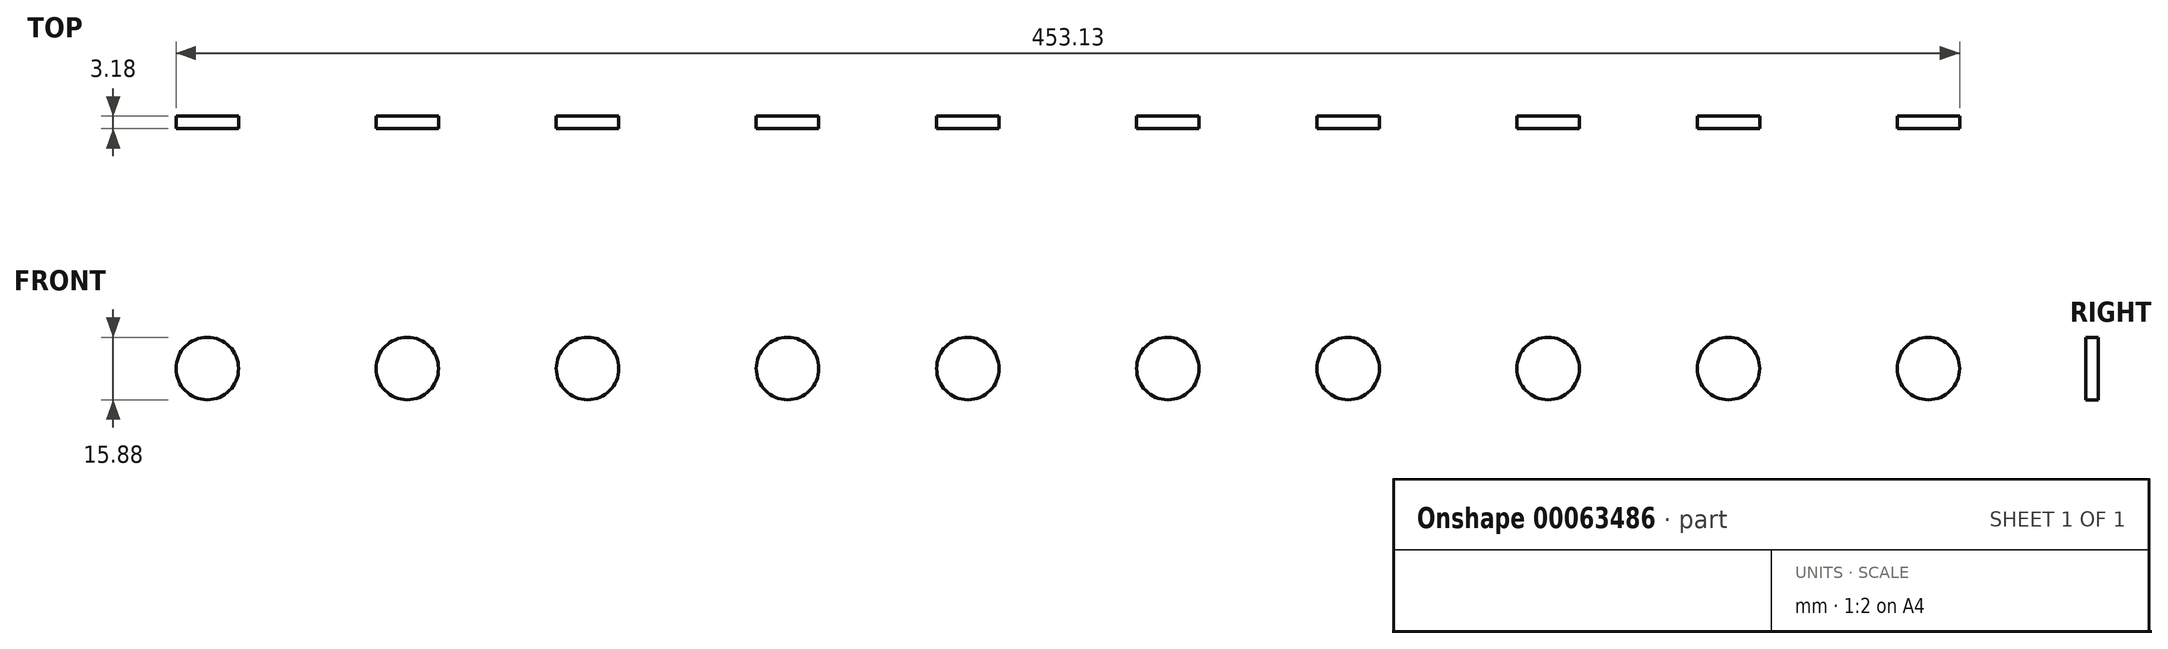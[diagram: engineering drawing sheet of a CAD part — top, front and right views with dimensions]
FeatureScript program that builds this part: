
annotation { "Feature Type Name" : "Feature", "Feature Type Description" : "" }
export const myFeature = defineFeature(function(context is Context, id is Id, definition is map)
    precondition{}
    {
        {
            var Q0;
            Q0=qCreatedBy(makeId("Front.planeOp"),FACE);
            var sketch = newSketch(context, id + "F0", { "sketchPlane" : qUnion([Q0])});
            skLineSegment(sketch, "E0.bottom", {"start": v(-400.95, 39.66) * mm, "end": v(684.9, 39.66) * mm});
            skLineSegment(sketch, "E0.top", {"start": v(-400.95, 14.26) * mm, "end": v(684.9, 14.26) * mm});
            skLineSegment(sketch, "E0.left", {"start": v(-400.95, 39.66) * mm, "end": v(-400.95, 14.26) * mm});
            skLineSegment(sketch, "E0.right", {"start": v(684.9, 39.66) * mm, "end": v(684.9, 14.26) * mm});
            skSolve(sketch);
        }
        {
            var Q0;
            Q0=makeQuery(id+"F0.imprint","IMPRINT",FACE,{"disambiguationData":[TD([[makeQuery(id+"F0.imprint","IMPRINT",EDGE,{"derivedFrom":sQuery(id+"F0.wireOp",EDGE,"E0.bottom")}),-1.0]])]});
            extrude(context, id + "F1", {"entities" : qUnion([Q0]), "depth" : 12.7 * mm});
        }
        {
            var Q0;
            Q0=makeQuery(id+"F1.opExtrude","SWEPT_FACE",FACE,{"disambiguationData":[OSD([sQuery(id+"F0.wireOp",EDGE,"E0.left")])]});
            var sketch = newSketch(context, id + "F2", { "sketchPlane" : qUnion([Q0])});
            skLineSegment(sketch, "E1.0", {"start": v(12.7, 39.66) * mm, "end": v(0, 39.66) * mm});
            skLineSegment(sketch, "E1.1", {"start": v(12.7, 39.66) * mm, "end": v(12.7, 14.26) * mm});
            skLineSegment(sketch, "E1.2", {"start": v(12.7, 14.26) * mm, "end": v(0, 14.26) * mm});
            skLineSegment(sketch, "E2.0", {"start": v(9.53, 36.48) * mm, "end": v(0, 36.48) * mm});
            skLineSegment(sketch, "E2.1", {"start": v(9.53, 36.48) * mm, "end": v(9.53, 17.43) * mm});
            skLineSegment(sketch, "E2.2", {"start": v(9.53, 17.43) * mm, "end": v(0, 17.43) * mm});
            skLineSegment(sketch, "E3.0", {"start": v(0, 39.66) * mm, "end": v(0, 14.26) * mm});
            skSolve(sketch);
        }
        {
            var Q0;
            {var subQ0=sQuery(id+"F2.wireOp",EDGE,"E2.0");Q0=makeQuery(id+"F2.imprint","IMPRINT",FACE,{"disambiguationData":[TD([[makeQuery(id+"F2.imprint","IMPRINT",EDGE,{"derivedFrom":subQ0}),1.0]])]});}
            extrude(context, id + "F3", {"entities" : qUnion([Q0]), "operationType" : NewBodyOperationType.REMOVE, "endBound" : BoundingType.THROUGH_ALL, "oppositeDirection" : true, "depth" : 25.4 * mm});
        }
        {
            var Q0;
            Q0=makeQuery(id+"F1.opExtrude","CAP_FACE",FACE,{"disambiguationData":[OSD([sQuery(id+"F0.wireOp",EDGE,"E0.bottom"),sQuery(id+"F0.wireOp",EDGE,"E0.top"),sQuery(id+"F0.wireOp",EDGE,"E0.left"),sQuery(id+"F0.wireOp",EDGE,"E0.right")])],"isStart":false});
            var sketch = newSketch(context, id + "F4", { "sketchPlane" : qUnion([Q0])});
            skLineSegment(sketch, "E4.0", {"start": v(-400.95, 39.66) * mm, "end": v(-400.95, 14.26) * mm});
            skLineSegment(sketch, "E4.1", {"start": v(-400.95, 39.66) * mm, "end": v(684.9, 39.66) * mm});
            skLineSegment(sketch, "E4.2", {"start": v(-400.95, 14.26) * mm, "end": v(684.9, 14.26) * mm});
            skLineSegment(sketch, "E4.3", {"start": v(684.9, 39.66) * mm, "end": v(684.9, 14.26) * mm});
            skLineSegment(sketch, "E5", {"start": v(-400.95, 26.96) * mm, "end": v(684.9, 26.96) * mm, "construction": true});
            skLineSegment(sketch, "E6", {"start": v(141.98, -83.16) * mm, "end": v(141.98, 205.53) * mm, "construction": true});
            skCircle(sketch, "E7", {"center": v(-366.48, 26.96) * mm, "radius": 7.94 * mm});
            skCircle(sketch, "E8", {"center": v(-315.68, 26.96) * mm, "radius": 7.94 * mm});
            skLineSegment(sketch, "E9", {"start": v(-366.48, 34.9) * mm, "end": v(-315.68, 34.9) * mm});
            skLineSegment(sketch, "E10", {"start": v(-366.48, 19.02) * mm, "end": v(-315.68, 19.02) * mm});
            skLineSegment(sketch, "E11.1.0.0", {"start": v(-269.87, 34.9) * mm, "end": v(-219.07, 34.9) * mm});
            skCircle(sketch, "E11.1.0.1", {"center": v(-269.87, 26.96) * mm, "radius": 7.94 * mm});
            skLineSegment(sketch, "E11.1.0.2", {"start": v(-269.87, 19.02) * mm, "end": v(-219.07, 19.02) * mm});
            skCircle(sketch, "E11.1.0.3", {"center": v(-219.07, 26.96) * mm, "radius": 7.94 * mm});
            skLineSegment(sketch, "E11.2.0.0", {"start": v(-173.26, 34.9) * mm, "end": v(-122.46, 34.9) * mm});
            skCircle(sketch, "E11.2.0.1", {"center": v(-173.26, 26.96) * mm, "radius": 7.94 * mm});
            skLineSegment(sketch, "E11.2.0.2", {"start": v(-173.26, 19.02) * mm, "end": v(-122.46, 19.02) * mm});
            skCircle(sketch, "E11.2.0.3", {"center": v(-122.46, 26.96) * mm, "radius": 7.94 * mm});
            skLineSegment(sketch, "E11.3.0.0", {"start": v(-76.65, 34.9) * mm, "end": v(-25.85, 34.9) * mm});
            skCircle(sketch, "E11.3.0.1", {"center": v(-76.65, 26.96) * mm, "radius": 7.94 * mm});
            skLineSegment(sketch, "E11.3.0.2", {"start": v(-76.65, 19.02) * mm, "end": v(-25.85, 19.02) * mm});
            skCircle(sketch, "E11.3.0.3", {"center": v(-25.85, 26.96) * mm, "radius": 7.94 * mm});
            skLineSegment(sketch, "E11.4.0.0", {"start": v(19.97, 34.9) * mm, "end": v(70.77, 34.9) * mm});
            skCircle(sketch, "E11.4.0.1", {"center": v(19.97, 26.96) * mm, "radius": 7.94 * mm});
            skLineSegment(sketch, "E11.4.0.2", {"start": v(19.97, 19.02) * mm, "end": v(70.77, 19.02) * mm});
            skCircle(sketch, "E11.4.0.3", {"center": v(70.77, 26.96) * mm, "radius": 7.94 * mm});
            skLineSegment(sketch, "E11.5.0.0", {"start": v(116.58, 34.9) * mm, "end": v(167.38, 34.9) * mm});
            skCircle(sketch, "E11.5.0.1", {"center": v(116.58, 26.96) * mm, "radius": 7.94 * mm});
            skLineSegment(sketch, "E11.5.0.2", {"start": v(116.58, 19.02) * mm, "end": v(167.38, 19.02) * mm});
            skCircle(sketch, "E11.5.0.3", {"center": v(167.38, 26.96) * mm, "radius": 7.94 * mm});
            skLineSegment(sketch, "E11.direction1", {"start": v(-366.48, 34.9) * mm, "end": v(-269.87, 34.9) * mm, "construction": true});
            skLineSegment(sketch, "E12", {"start": v(141.98, 34.9) * mm, "end": v(141.98, 19.02) * mm});
            skCircle(sketch, "E13.MirrorC", {"center": v(650.44, 26.96) * mm, "radius": 7.94 * mm});
            skLineSegment(sketch, "E14.MirrorCS", {"start": v(650.44, 34.9) * mm, "end": v(599.64, 34.9) * mm});
            skLineSegment(sketch, "E15.MirrorCS", {"start": v(650.44, 19.02) * mm, "end": v(599.64, 19.02) * mm});
            skCircle(sketch, "E16.MirrorC", {"center": v(599.64, 26.96) * mm, "radius": 7.94 * mm});
            skCircle(sketch, "E17.MirrorC", {"center": v(213.2, 26.96) * mm, "radius": 7.94 * mm});
            skLineSegment(sketch, "E18.MirrorCS", {"start": v(264, 34.9) * mm, "end": v(213.2, 34.9) * mm});
            skLineSegment(sketch, "E19.MirrorCS", {"start": v(264, 19.02) * mm, "end": v(213.2, 19.02) * mm});
            skCircle(sketch, "E20.MirrorC", {"center": v(264, 26.96) * mm, "radius": 7.94 * mm});
            skCircle(sketch, "E21.MirrorC", {"center": v(309.8, 26.96) * mm, "radius": 7.94 * mm});
            skLineSegment(sketch, "E22.MirrorCS", {"start": v(360.6, 34.9) * mm, "end": v(309.8, 34.9) * mm});
            skLineSegment(sketch, "E23.MirrorCS", {"start": v(360.6, 19.02) * mm, "end": v(309.8, 19.02) * mm});
            skCircle(sketch, "E24.MirrorC", {"center": v(360.6, 26.96) * mm, "radius": 7.94 * mm});
            skCircle(sketch, "E25.MirrorC", {"center": v(406.42, 26.96) * mm, "radius": 7.94 * mm});
            skLineSegment(sketch, "E26.MirrorCS", {"start": v(457.22, 34.9) * mm, "end": v(406.42, 34.9) * mm});
            skLineSegment(sketch, "E27.MirrorCS", {"start": v(457.22, 19.02) * mm, "end": v(406.42, 19.02) * mm});
            skCircle(sketch, "E28.MirrorC", {"center": v(457.22, 26.96) * mm, "radius": 7.94 * mm});
            skCircle(sketch, "E29.MirrorC", {"center": v(553.83, 26.96) * mm, "radius": 7.94 * mm});
            skLineSegment(sketch, "E30.MirrorCS", {"start": v(553.83, 34.9) * mm, "end": v(503.03, 34.9) * mm});
            skLineSegment(sketch, "E31.MirrorCS", {"start": v(553.83, 19.02) * mm, "end": v(503.03, 19.02) * mm});
            skCircle(sketch, "E32.MirrorC", {"center": v(503.03, 26.96) * mm, "radius": 7.94 * mm});
            skSolve(sketch);
        }
        {
            var Q0;
            {var subQ0=sQuery(id+"F4.wireOp",EDGE,"E7");var subQ1=makeQuery(id+"F4.imprint","INTERSECT",VERTEX,{"derivedFrom":[subQ0,sQuery(id+"F4.wireOp",EDGE,"E9")]});Q0=makeQuery(id+"F4.imprint","IMPRINT",FACE,{"disambiguationData":[TD([[makeQuery(id+"F4.imprint","IMPRINT",EDGE,{"disambiguationData":[TD([[subQ1,-1.0]])],"derivedFrom":subQ0}),1.0]])]});}
            var Q1;
            {var subQ0=sQuery(id+"F4.wireOp",EDGE,"E9");Q1=makeQuery(id+"F4.imprint","IMPRINT",FACE,{"disambiguationData":[TD([[makeQuery(id+"F4.imprint","IMPRINT",EDGE,{"derivedFrom":subQ0}),-1.0]])]});}
            var Q2;
            {var subQ0=sQuery(id+"F4.wireOp",EDGE,"E8");var subQ1=makeQuery(id+"F4.imprint","INTERSECT",VERTEX,{"derivedFrom":[subQ0,sQuery(id+"F4.wireOp",EDGE,"E9")]});Q2=makeQuery(id+"F4.imprint","IMPRINT",FACE,{"disambiguationData":[TD([[makeQuery(id+"F4.imprint","IMPRINT",EDGE,{"disambiguationData":[TD([[subQ1,-1.0]])],"derivedFrom":subQ0}),1.0]])]});}
            var Q3;
            {var subQ0=sQuery(id+"F4.wireOp",EDGE,"E11.1.0.1");var subQ1=makeQuery(id+"F4.imprint","INTERSECT",VERTEX,{"derivedFrom":[sQuery(id+"F4.wireOp",EDGE,"E11.1.0.0"),subQ0]});Q3=makeQuery(id+"F4.imprint","IMPRINT",FACE,{"disambiguationData":[TD([[makeQuery(id+"F4.imprint","IMPRINT",EDGE,{"disambiguationData":[TD([[subQ1,-1.0]])],"derivedFrom":subQ0}),1.0]])]});}
            var Q4;
            {var subQ0=sQuery(id+"F4.wireOp",EDGE,"E11.1.0.0");Q4=makeQuery(id+"F4.imprint","IMPRINT",FACE,{"disambiguationData":[TD([[makeQuery(id+"F4.imprint","IMPRINT",EDGE,{"derivedFrom":subQ0}),-1.0]])]});}
            var Q5;
            {var subQ0=sQuery(id+"F4.wireOp",EDGE,"E11.1.0.3");var subQ1=makeQuery(id+"F4.imprint","INTERSECT",VERTEX,{"derivedFrom":[sQuery(id+"F4.wireOp",EDGE,"E11.1.0.0"),subQ0]});Q5=makeQuery(id+"F4.imprint","IMPRINT",FACE,{"disambiguationData":[TD([[makeQuery(id+"F4.imprint","IMPRINT",EDGE,{"disambiguationData":[TD([[subQ1,-1.0]])],"derivedFrom":subQ0}),1.0]])]});}
            var Q6;
            {var subQ0=sQuery(id+"F4.wireOp",EDGE,"E11.2.0.1");var subQ1=makeQuery(id+"F4.imprint","INTERSECT",VERTEX,{"derivedFrom":[sQuery(id+"F4.wireOp",EDGE,"E11.2.0.0"),subQ0]});Q6=makeQuery(id+"F4.imprint","IMPRINT",FACE,{"disambiguationData":[TD([[makeQuery(id+"F4.imprint","IMPRINT",EDGE,{"disambiguationData":[TD([[subQ1,-1.0]])],"derivedFrom":subQ0}),1.0]])]});}
            var Q7;
            {var subQ0=sQuery(id+"F4.wireOp",EDGE,"E11.2.0.0");Q7=makeQuery(id+"F4.imprint","IMPRINT",FACE,{"disambiguationData":[TD([[makeQuery(id+"F4.imprint","IMPRINT",EDGE,{"derivedFrom":subQ0}),-1.0]])]});}
            var Q8;
            {var subQ0=sQuery(id+"F4.wireOp",EDGE,"E11.2.0.3");var subQ1=makeQuery(id+"F4.imprint","INTERSECT",VERTEX,{"derivedFrom":[sQuery(id+"F4.wireOp",EDGE,"E11.2.0.0"),subQ0]});Q8=makeQuery(id+"F4.imprint","IMPRINT",FACE,{"disambiguationData":[TD([[makeQuery(id+"F4.imprint","IMPRINT",EDGE,{"disambiguationData":[TD([[subQ1,-1.0]])],"derivedFrom":subQ0}),1.0]])]});}
            var Q9;
            {var subQ0=sQuery(id+"F4.wireOp",EDGE,"E11.3.0.1");var subQ1=makeQuery(id+"F4.imprint","INTERSECT",VERTEX,{"derivedFrom":[sQuery(id+"F4.wireOp",EDGE,"E11.3.0.0"),subQ0]});Q9=makeQuery(id+"F4.imprint","IMPRINT",FACE,{"disambiguationData":[TD([[makeQuery(id+"F4.imprint","IMPRINT",EDGE,{"disambiguationData":[TD([[subQ1,-1.0]])],"derivedFrom":subQ0}),1.0]])]});}
            var Q10;
            {var subQ0=sQuery(id+"F4.wireOp",EDGE,"E11.3.0.0");Q10=makeQuery(id+"F4.imprint","IMPRINT",FACE,{"disambiguationData":[TD([[makeQuery(id+"F4.imprint","IMPRINT",EDGE,{"derivedFrom":subQ0}),-1.0]])]});}
            var Q11;
            {var subQ0=sQuery(id+"F4.wireOp",EDGE,"E11.3.0.3");var subQ1=makeQuery(id+"F4.imprint","INTERSECT",VERTEX,{"derivedFrom":[sQuery(id+"F4.wireOp",EDGE,"E11.3.0.0"),subQ0]});Q11=makeQuery(id+"F4.imprint","IMPRINT",FACE,{"disambiguationData":[TD([[makeQuery(id+"F4.imprint","IMPRINT",EDGE,{"disambiguationData":[TD([[subQ1,-1.0]])],"derivedFrom":subQ0}),1.0]])]});}
            var Q12;
            {var subQ0=sQuery(id+"F4.wireOp",EDGE,"E11.4.0.1");var subQ1=makeQuery(id+"F4.imprint","INTERSECT",VERTEX,{"derivedFrom":[sQuery(id+"F4.wireOp",EDGE,"E11.4.0.0"),subQ0]});Q12=makeQuery(id+"F4.imprint","IMPRINT",FACE,{"disambiguationData":[TD([[makeQuery(id+"F4.imprint","IMPRINT",EDGE,{"disambiguationData":[TD([[subQ1,-1.0]])],"derivedFrom":subQ0}),1.0]])]});}
            var Q13;
            {var subQ0=sQuery(id+"F4.wireOp",EDGE,"E11.4.0.0");Q13=makeQuery(id+"F4.imprint","IMPRINT",FACE,{"disambiguationData":[TD([[makeQuery(id+"F4.imprint","IMPRINT",EDGE,{"derivedFrom":subQ0}),-1.0]])]});}
            var Q14;
            {var subQ0=sQuery(id+"F4.wireOp",EDGE,"E11.4.0.3");var subQ1=makeQuery(id+"F4.imprint","INTERSECT",VERTEX,{"derivedFrom":[sQuery(id+"F4.wireOp",EDGE,"E11.4.0.0"),subQ0]});Q14=makeQuery(id+"F4.imprint","IMPRINT",FACE,{"disambiguationData":[TD([[makeQuery(id+"F4.imprint","IMPRINT",EDGE,{"disambiguationData":[TD([[subQ1,-1.0]])],"derivedFrom":subQ0}),1.0]])]});}
            var Q15;
            {var subQ0=sQuery(id+"F4.wireOp",EDGE,"E11.5.0.1");var subQ1=makeQuery(id+"F4.imprint","INTERSECT",VERTEX,{"derivedFrom":[sQuery(id+"F4.wireOp",EDGE,"E11.5.0.0"),subQ0]});Q15=makeQuery(id+"F4.imprint","IMPRINT",FACE,{"disambiguationData":[TD([[makeQuery(id+"F4.imprint","IMPRINT",EDGE,{"disambiguationData":[TD([[subQ1,-1.0]])],"derivedFrom":subQ0}),1.0]])]});}
            var Q16;
            {var subQ3=sQuery(id+"F4.wireOp",EDGE,"E12");Q16=makeQuery(id+"F4.imprint","IMPRINT",FACE,{"disambiguationData":[TD([[makeQuery(id+"F4.imprint","IMPRINT",EDGE,{"derivedFrom":subQ3}),-1.0]])]});}
            var Q17;
            {var subQ3=sQuery(id+"F4.wireOp",EDGE,"E12");Q17=makeQuery(id+"F4.imprint","IMPRINT",FACE,{"disambiguationData":[TD([[makeQuery(id+"F4.imprint","IMPRINT",EDGE,{"derivedFrom":subQ3}),1.0]])]});}
            var Q18;
            {var subQ0=sQuery(id+"F4.wireOp",EDGE,"E11.5.0.3");var subQ1=makeQuery(id+"F4.imprint","INTERSECT",VERTEX,{"derivedFrom":[sQuery(id+"F4.wireOp",EDGE,"E11.5.0.0"),subQ0]});Q18=makeQuery(id+"F4.imprint","IMPRINT",FACE,{"disambiguationData":[TD([[makeQuery(id+"F4.imprint","IMPRINT",EDGE,{"disambiguationData":[TD([[subQ1,-1.0]])],"derivedFrom":subQ0}),1.0]])]});}
            var Q19;
            {var subQ0=sQuery(id+"F4.wireOp",EDGE,"E17.MirrorC");var subQ1=makeQuery(id+"F4.imprint","INTERSECT",VERTEX,{"derivedFrom":[subQ0,sQuery(id+"F4.wireOp",EDGE,"E18.MirrorCS")]});Q19=makeQuery(id+"F4.imprint","IMPRINT",FACE,{"disambiguationData":[TD([[makeQuery(id+"F4.imprint","IMPRINT",EDGE,{"disambiguationData":[TD([[subQ1,-1.0]])],"derivedFrom":subQ0}),-1.0]])]});}
            var Q20;
            {var subQ0=sQuery(id+"F4.wireOp",EDGE,"E18.MirrorCS");Q20=makeQuery(id+"F4.imprint","IMPRINT",FACE,{"disambiguationData":[TD([[makeQuery(id+"F4.imprint","IMPRINT",EDGE,{"derivedFrom":subQ0}),1.0]])]});}
            var Q21;
            {var subQ0=sQuery(id+"F4.wireOp",EDGE,"E20.MirrorC");var subQ1=makeQuery(id+"F4.imprint","INTERSECT",VERTEX,{"derivedFrom":[sQuery(id+"F4.wireOp",EDGE,"E18.MirrorCS"),subQ0]});Q21=makeQuery(id+"F4.imprint","IMPRINT",FACE,{"disambiguationData":[TD([[makeQuery(id+"F4.imprint","IMPRINT",EDGE,{"disambiguationData":[TD([[subQ1,-1.0]])],"derivedFrom":subQ0}),-1.0]])]});}
            var Q22;
            {var subQ0=sQuery(id+"F4.wireOp",EDGE,"E21.MirrorC");var subQ1=makeQuery(id+"F4.imprint","INTERSECT",VERTEX,{"derivedFrom":[subQ0,sQuery(id+"F4.wireOp",EDGE,"E22.MirrorCS")]});Q22=makeQuery(id+"F4.imprint","IMPRINT",FACE,{"disambiguationData":[TD([[makeQuery(id+"F4.imprint","IMPRINT",EDGE,{"disambiguationData":[TD([[subQ1,-1.0]])],"derivedFrom":subQ0}),-1.0]])]});}
            var Q23;
            {var subQ0=sQuery(id+"F4.wireOp",EDGE,"E22.MirrorCS");Q23=makeQuery(id+"F4.imprint","IMPRINT",FACE,{"disambiguationData":[TD([[makeQuery(id+"F4.imprint","IMPRINT",EDGE,{"derivedFrom":subQ0}),1.0]])]});}
            var Q24;
            {var subQ0=sQuery(id+"F4.wireOp",EDGE,"E24.MirrorC");var subQ1=makeQuery(id+"F4.imprint","INTERSECT",VERTEX,{"derivedFrom":[sQuery(id+"F4.wireOp",EDGE,"E22.MirrorCS"),subQ0]});Q24=makeQuery(id+"F4.imprint","IMPRINT",FACE,{"disambiguationData":[TD([[makeQuery(id+"F4.imprint","IMPRINT",EDGE,{"disambiguationData":[TD([[subQ1,-1.0]])],"derivedFrom":subQ0}),-1.0]])]});}
            var Q25;
            {var subQ0=sQuery(id+"F4.wireOp",EDGE,"E25.MirrorC");var subQ1=makeQuery(id+"F4.imprint","INTERSECT",VERTEX,{"derivedFrom":[subQ0,sQuery(id+"F4.wireOp",EDGE,"E26.MirrorCS")]});Q25=makeQuery(id+"F4.imprint","IMPRINT",FACE,{"disambiguationData":[TD([[makeQuery(id+"F4.imprint","IMPRINT",EDGE,{"disambiguationData":[TD([[subQ1,-1.0]])],"derivedFrom":subQ0}),-1.0]])]});}
            var Q26;
            {var subQ0=sQuery(id+"F4.wireOp",EDGE,"E26.MirrorCS");Q26=makeQuery(id+"F4.imprint","IMPRINT",FACE,{"disambiguationData":[TD([[makeQuery(id+"F4.imprint","IMPRINT",EDGE,{"derivedFrom":subQ0}),1.0]])]});}
            var Q27;
            {var subQ0=sQuery(id+"F4.wireOp",EDGE,"E28.MirrorC");var subQ1=makeQuery(id+"F4.imprint","INTERSECT",VERTEX,{"derivedFrom":[sQuery(id+"F4.wireOp",EDGE,"E26.MirrorCS"),subQ0]});Q27=makeQuery(id+"F4.imprint","IMPRINT",FACE,{"disambiguationData":[TD([[makeQuery(id+"F4.imprint","IMPRINT",EDGE,{"disambiguationData":[TD([[subQ1,-1.0]])],"derivedFrom":subQ0}),-1.0]])]});}
            var Q28;
            {var subQ0=sQuery(id+"F4.wireOp",EDGE,"E32.MirrorC");var subQ1=makeQuery(id+"F4.imprint","INTERSECT",VERTEX,{"derivedFrom":[sQuery(id+"F4.wireOp",EDGE,"E30.MirrorCS"),subQ0]});Q28=makeQuery(id+"F4.imprint","IMPRINT",FACE,{"disambiguationData":[TD([[makeQuery(id+"F4.imprint","IMPRINT",EDGE,{"disambiguationData":[TD([[subQ1,-1.0]])],"derivedFrom":subQ0}),-1.0]])]});}
            var Q29;
            {var subQ0=sQuery(id+"F4.wireOp",EDGE,"E30.MirrorCS");Q29=makeQuery(id+"F4.imprint","IMPRINT",FACE,{"disambiguationData":[TD([[makeQuery(id+"F4.imprint","IMPRINT",EDGE,{"derivedFrom":subQ0}),1.0]])]});}
            var Q30;
            {var subQ0=sQuery(id+"F4.wireOp",EDGE,"E29.MirrorC");var subQ1=makeQuery(id+"F4.imprint","INTERSECT",VERTEX,{"derivedFrom":[subQ0,sQuery(id+"F4.wireOp",EDGE,"E30.MirrorCS")]});Q30=makeQuery(id+"F4.imprint","IMPRINT",FACE,{"disambiguationData":[TD([[makeQuery(id+"F4.imprint","IMPRINT",EDGE,{"disambiguationData":[TD([[subQ1,-1.0]])],"derivedFrom":subQ0}),-1.0]])]});}
            var Q31;
            {var subQ0=sQuery(id+"F4.wireOp",EDGE,"E16.MirrorC");var subQ1=makeQuery(id+"F4.imprint","INTERSECT",VERTEX,{"derivedFrom":[sQuery(id+"F4.wireOp",EDGE,"E14.MirrorCS"),subQ0]});Q31=makeQuery(id+"F4.imprint","IMPRINT",FACE,{"disambiguationData":[TD([[makeQuery(id+"F4.imprint","IMPRINT",EDGE,{"disambiguationData":[TD([[subQ1,-1.0]])],"derivedFrom":subQ0}),-1.0]])]});}
            var Q32;
            {var subQ0=sQuery(id+"F4.wireOp",EDGE,"E14.MirrorCS");Q32=makeQuery(id+"F4.imprint","IMPRINT",FACE,{"disambiguationData":[TD([[makeQuery(id+"F4.imprint","IMPRINT",EDGE,{"derivedFrom":subQ0}),1.0]])]});}
            var Q33;
            {var subQ0=sQuery(id+"F4.wireOp",EDGE,"E13.MirrorC");var subQ1=makeQuery(id+"F4.imprint","INTERSECT",VERTEX,{"derivedFrom":[subQ0,sQuery(id+"F4.wireOp",EDGE,"E14.MirrorCS")]});Q33=makeQuery(id+"F4.imprint","IMPRINT",FACE,{"disambiguationData":[TD([[makeQuery(id+"F4.imprint","IMPRINT",EDGE,{"disambiguationData":[TD([[subQ1,-1.0]])],"derivedFrom":subQ0}),-1.0]])]});}
            extrude(context, id + "F5", {"entities" : qUnion([Q0, Q1, Q2, Q3, Q4, Q5, Q6, Q7, Q8, Q9, Q10, Q11, Q12, Q13, Q14, Q15, Q16, Q17, Q18, Q19, Q20, Q21, Q22, Q23, Q24, Q25, Q26, Q27, Q28, Q29, Q30, Q31, Q32, Q33]), "operationType" : NewBodyOperationType.REMOVE, "endBound" : BoundingType.THROUGH_ALL, "oppositeDirection" : true, "depth" : 25.4 * mm});
        }
    });
